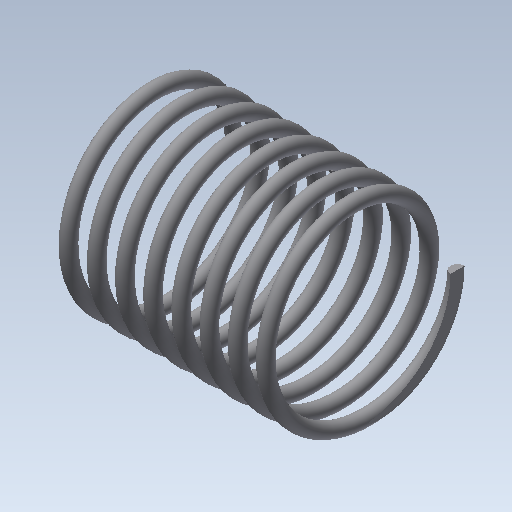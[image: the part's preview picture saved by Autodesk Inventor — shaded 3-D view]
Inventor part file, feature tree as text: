
AUTODESK INVENTOR PART (.ipt)
format: ipt  version: 2020 (Build 240168000, 168)  size: 465,920 bytes
history: native  units: mm
features: sketch x2, helix x1, extrude x1, projected_geometry x1
ambient origin geometry x8: Origin, YZ Plane, XZ Plane, XY Plane, X Axis, Y Axis, Z Axis, Center Point
bodies: Solid1 (feature_tree)
feature tree (5):
  helix  "Coil1"  [1 undecoded]
  extrude  "Extrusion1"  TaperAngle=0.0deg  [1 undecoded]
  sketch  "Sketch1"  dims[d1=7.875mm d2=0.0mm]
  sketch  "Sketch2"  dims[d3=20.0mm d4=2.5mm d5=10.0mm d6=80.0mm d7=0.0mm d8=90.0deg d9=90.0deg d10=0.0mm d11=0.0mm d12=20.0mm d13=10.0mm d14=51.25mm d15=0.0mm]
  projected_geometry  "Project Cut Edges1"
note: 2 required parameter values undecoded (feature->parameter linkage not recoverable at this tier; creation-order binding heuristic only, values carry confidence <= 0.55)
